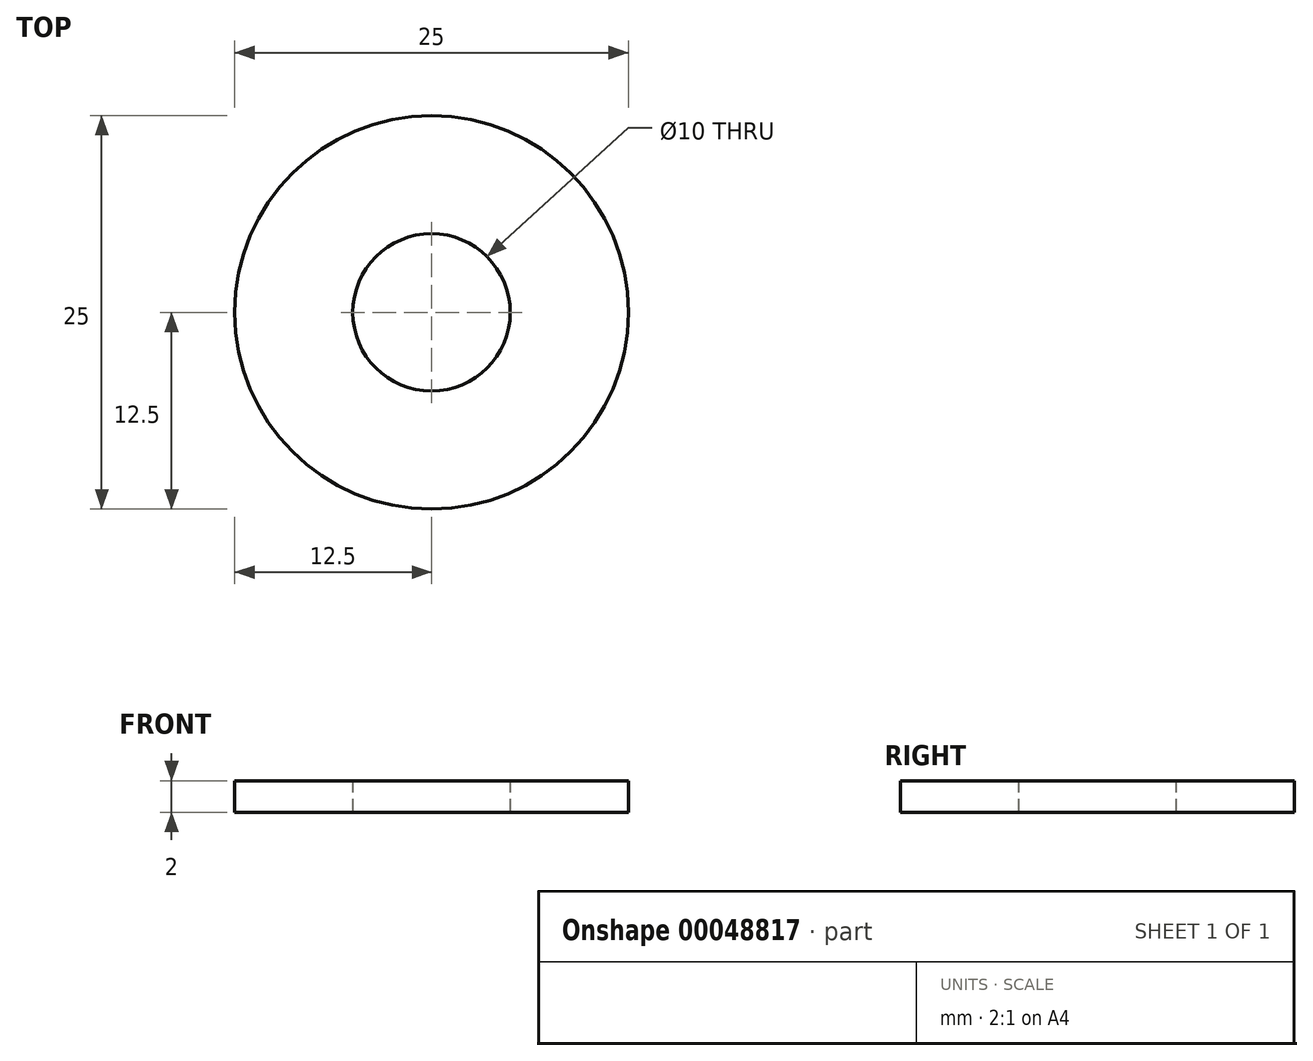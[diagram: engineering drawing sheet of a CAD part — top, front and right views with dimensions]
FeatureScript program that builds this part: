
annotation { "Feature Type Name" : "Feature", "Feature Type Description" : "" }
export const myFeature = defineFeature(function(context is Context, id is Id, definition is map)
    precondition{}
    {
        {
            var Q0;
            Q0=qCreatedBy(makeId("Top.planeOp"),FACE);
            var sketch = newSketch(context, id + "F0", { "sketchPlane" : qUnion([Q0])});
            skCircle(sketch, "E0", {"center": v(0, 0) * mm, "radius": 5 * mm});
            skCircle(sketch, "E1", {"center": v(0, 0) * mm, "radius": 12.5 * mm});
            skSolve(sketch);
        }
        {
            var Q0;
            Q0=makeQuery(id+"F0.imprint","IMPRINT",FACE,{"disambiguationData":[TD([[makeQuery(id+"F0.imprint","IMPRINT",EDGE,{"derivedFrom":sQuery(id+"F0.wireOp",EDGE,"E0")}),-1.0]])]});
            extrude(context, id + "F1", {"entities" : qUnion([Q0]), "depth" : 2 * mm, "offsetDistance" : 25 * mm});
        }
    });
